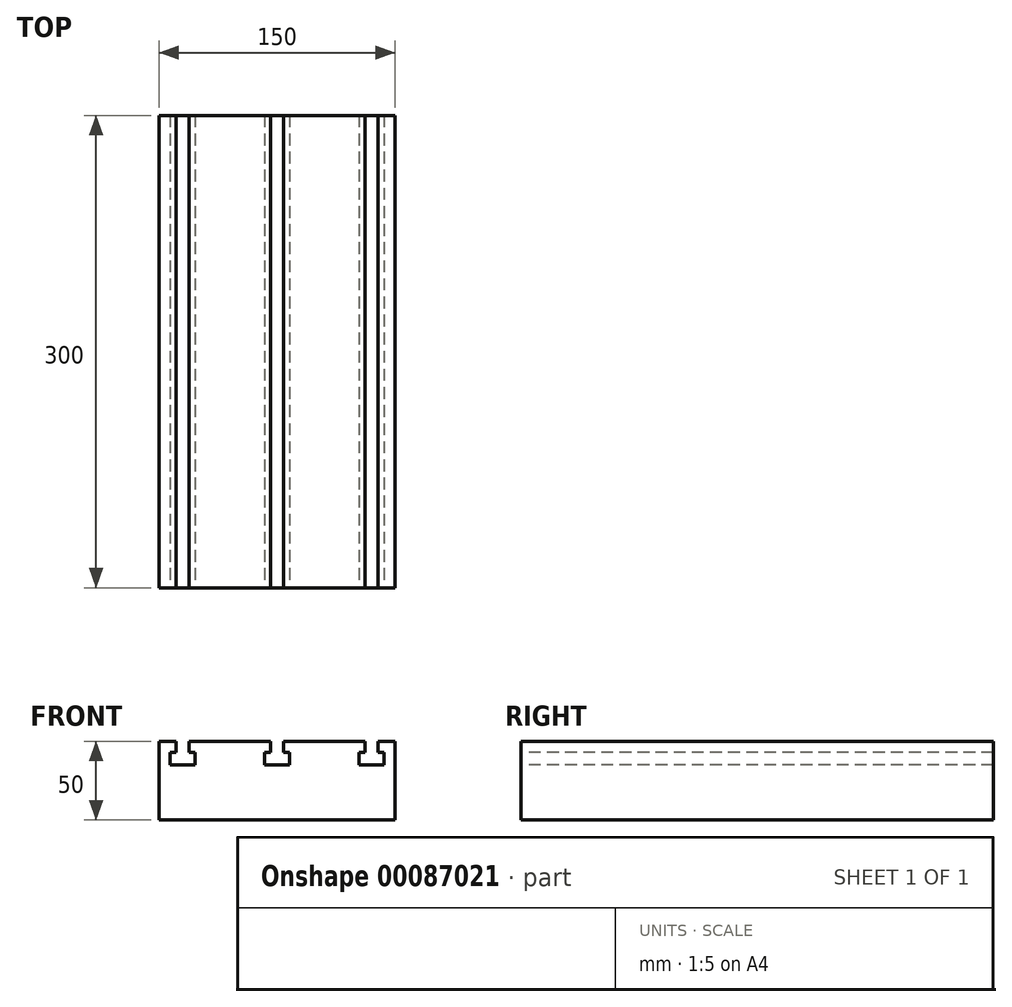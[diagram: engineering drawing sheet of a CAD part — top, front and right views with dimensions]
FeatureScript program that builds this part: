
annotation { "Feature Type Name" : "Feature", "Feature Type Description" : "" }
export const myFeature = defineFeature(function(context is Context, id is Id, definition is map)
    precondition{}
    {
        {
            var Q0;
            Q0=qCreatedBy(makeId("Front.planeOp"),FACE);
            var sketch = newSketch(context, id + "F0", { "sketchPlane" : qUnion([Q0])});
            skLineSegment(sketch, "E0.bottom", {"start": v(-75, -25) * mm, "end": v(75, -25) * mm});
            skLineSegment(sketch, "E0.top", {"start": v(-75, 25) * mm, "end": v(-64.2, 25) * mm});
            skLineSegment(sketch, "E0.left", {"start": v(-75, -25) * mm, "end": v(-75, 25) * mm});
            skLineSegment(sketch, "E0.right", {"start": v(75, -25) * mm, "end": v(75, 25) * mm});
            skPoint(sketch, "E0.middle", {"position": v(0, 0) * mm});
            skLineSegment(sketch, "E1.bottom", {"start": v(-8, 10) * mm, "end": v(8, 10) * mm});
            skLineSegment(sketch, "E1.top", {"start": v(-8, 18) * mm, "end": v(-4.2, 18) * mm});
            skLineSegment(sketch, "E1.left", {"start": v(-8, 10) * mm, "end": v(-8, 18) * mm});
            skLineSegment(sketch, "E1.right", {"start": v(8, 10) * mm, "end": v(8, 18) * mm});
            skPoint(sketch, "E1.middle", {"position": v(0, 14) * mm});
            skLineSegment(sketch, "E2", {"start": v(-4.2, 18) * mm, "end": v(-4.2, 25) * mm});
            skLineSegment(sketch, "E3.MirrorCS", {"start": v(4.2, 18) * mm, "end": v(4.2, 25) * mm});
            skPoint(sketch, "E4.orphan", {"position": v(-4.2, 32.97) * mm});
            skPoint(sketch, "E5.orphan", {"position": v(4.2, 32.97) * mm});
            skLineSegment(sketch, "E6.trimOffspring", {"start": v(4.2, 25) * mm, "end": v(55.8, 25) * mm});
            skLineSegment(sketch, "E7.trimOffspring", {"start": v(4.2, 18) * mm, "end": v(8, 18) * mm});
            skLineSegment(sketch, "E8.1.0.0", {"start": v(55.8, 18) * mm, "end": v(55.8, 25) * mm});
            skLineSegment(sketch, "E8.1.0.1", {"start": v(64.2, 18) * mm, "end": v(64.2, 25) * mm});
            skLineSegment(sketch, "E8.1.0.2", {"start": v(52, 10) * mm, "end": v(68, 10) * mm});
            skLineSegment(sketch, "E8.1.0.3", {"start": v(68, 10) * mm, "end": v(68, 18) * mm});
            skLineSegment(sketch, "E8.1.0.4", {"start": v(52, 10) * mm, "end": v(52, 18) * mm});
            skPoint(sketch, "E8.1.0.5", {"position": v(60, 14) * mm});
            skLineSegment(sketch, "E8.1.0.6", {"start": v(52, 18) * mm, "end": v(55.8, 18) * mm});
            skLineSegment(sketch, "E8.1.0.7", {"start": v(64.2, 18) * mm, "end": v(68, 18) * mm});
            skLineSegment(sketch, "E8.direction1", {"start": v(-4.2, 18) * mm, "end": v(55.8, 18) * mm, "construction": true});
            skLineSegment(sketch, "E9.trimOffspring", {"start": v(64.2, 25) * mm, "end": v(75, 25) * mm});
            skLineSegment(sketch, "E10.MirrorCS", {"start": v(-68, 10) * mm, "end": v(-68, 18) * mm});
            skPoint(sketch, "E11.MirrorP", {"position": v(-60, 14) * mm});
            skLineSegment(sketch, "E12.MirrorCS", {"start": v(-52, 10) * mm, "end": v(-68, 10) * mm});
            skLineSegment(sketch, "E13.MirrorCS", {"start": v(-52, 18) * mm, "end": v(-55.8, 18) * mm});
            skLineSegment(sketch, "E14.MirrorCS", {"start": v(-64.2, 18) * mm, "end": v(-68, 18) * mm});
            skLineSegment(sketch, "E15.MirrorCS", {"start": v(-52, 10) * mm, "end": v(-52, 18) * mm});
            skLineSegment(sketch, "E16.MirrorCS", {"start": v(-55.8, 18) * mm, "end": v(-55.8, 25) * mm});
            skLineSegment(sketch, "E17.MirrorCS", {"start": v(-64.2, 18) * mm, "end": v(-64.2, 25) * mm});
            skLineSegment(sketch, "E18.trimOffspring", {"start": v(-55.8, 25) * mm, "end": v(-4.2, 25) * mm});
            skSolve(sketch);
        }
        {
            var Q0;
            Q0=makeQuery(id+"F0.imprint","IMPRINT",FACE,{"disambiguationData":[TD([[makeQuery(id+"F0.imprint","IMPRINT",EDGE,{"derivedFrom":sQuery(id+"F0.wireOp",EDGE,"E0.bottom")}),1.0]])]});
            extrude(context, id + "F1", {"entities" : qUnion([Q0]), "oppositeDirection" : true, "depth" : 150 * mm, "hasSecondDirection" : true, "secondDirectionOppositeDirection" : false, "secondDirectionDepth" : 150 * mm});
        }
    });
